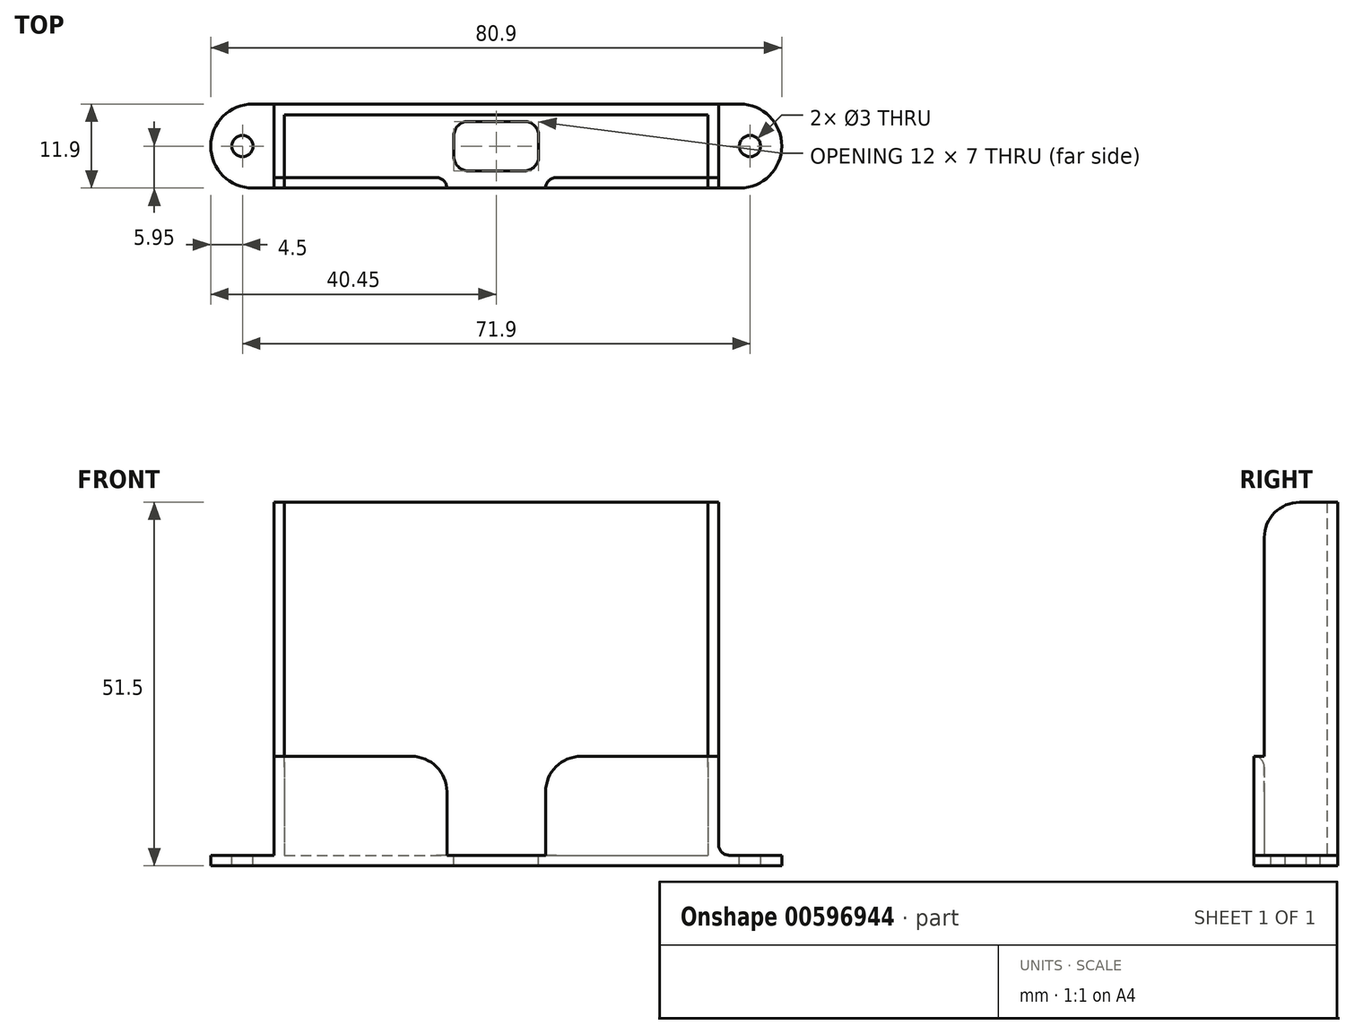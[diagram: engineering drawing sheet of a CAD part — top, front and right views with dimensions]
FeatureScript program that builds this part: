
annotation { "Feature Type Name" : "Feature", "Feature Type Description" : "" }
export const myFeature = defineFeature(function(context is Context, id is Id, definition is map)
    precondition{}
    {
        {
            assignVariable(context, id + "F0", {"name" : "THK", "anyValue" : 1.5});
        }
        {
            var Q0;
            Q0=qCreatedBy(makeId("Top.planeOp"),FACE);
            var sketch = newSketch(context, id + "F1", { "sketchPlane" : qUnion([Q0])});
            skLineSegment(sketch, "E0.bottom", {"start": v(-61.5, -1.5) * mm, "end": v(-1.5, -1.5) * mm});
            skLineSegment(sketch, "E0.top", {"start": v(-61.5, -10.4) * mm, "end": v(-1.5, -10.4) * mm});
            skLineSegment(sketch, "E0.left", {"start": v(-61.5, -1.5) * mm, "end": v(-61.5, -10.4) * mm});
            skLineSegment(sketch, "E0.right", {"start": v(-1.5, -1.5) * mm, "end": v(-1.5, -10.4) * mm});
            skLineSegment(sketch, "E1.0", {"start": v(-63, 0) * mm, "end": v(0, 0) * mm});
            skLineSegment(sketch, "E1.1", {"start": v(-63, 0) * mm, "end": v(-63, -11.9) * mm});
            skLineSegment(sketch, "E1.2", {"start": v(-63, -11.9) * mm, "end": v(0, -11.9) * mm});
            skLineSegment(sketch, "E1.3", {"start": v(0, 0) * mm, "end": v(0, -11.9) * mm});
            skLineSegment(sketch, "E2", {"start": v(-1.5, -10.4) * mm, "end": v(0, -10.4) * mm});
            skLineSegment(sketch, "E3", {"start": v(-61.5, -10.4) * mm, "end": v(-63, -10.4) * mm});
            skLineSegment(sketch, "E4", {"start": v(-31.5, -1.5) * mm, "end": v(-31.5, -10.4) * mm, "construction": true});
            skLineSegment(sketch, "E5", {"start": v(-63, 0) * mm, "end": v(-66, 0) * mm});
            skLineSegment(sketch, "E6", {"start": v(0, 0) * mm, "end": v(3, 0) * mm});
            skLineSegment(sketch, "E7", {"start": v(0, -11.9) * mm, "end": v(3, -11.9) * mm});
            skLineSegment(sketch, "E8", {"start": v(-63, -11.9) * mm, "end": v(-66, -11.9) * mm});
            skArc(sketch, "E9", {"start": v(-66, 0) * mm, "mid": v(-71.95, -5.95) * mm, "end": v(-66, -11.9) * mm});
            skArc(sketch, "E10", {"start": v(3, 0) * mm, "mid": v(8.95, -5.95) * mm, "end": v(3, -11.9) * mm});
            skLineSegment(sketch, "E11", {"start": v(-71.95, -5.95) * mm, "end": v(8.95, -5.95) * mm, "construction": true});
            skCircle(sketch, "E12", {"center": v(-67.45, -5.95) * mm, "radius": 1.5 * mm});
            skCircle(sketch, "E13.MirrorC", {"center": v(4.45, -5.95) * mm, "radius": 1.5 * mm});
            skLineSegment(sketch, "E14", {"start": v(-24.5, -10.4) * mm, "end": v(-24.5, -11.9) * mm});
            skLineSegment(sketch, "E15", {"start": v(-38.5, -10.4) * mm, "end": v(-38.5, -11.9) * mm});
            skLineSegment(sketch, "E16", {"start": v(-35.5, -2.45) * mm, "end": v(-27.5, -2.45) * mm});
            skLineSegment(sketch, "E17", {"start": v(-27.5, -9.45) * mm, "end": v(-35.5, -9.45) * mm});
            skPoint(sketch, "E18", {"position": v(-31.5, -2.45) * mm});
            skLineSegment(sketch, "E19", {"start": v(-37.5, -4.45) * mm, "end": v(-37.5, -7.45) * mm});
            skLineSegment(sketch, "E20", {"start": v(-25.5, -4.45) * mm, "end": v(-25.5, -7.45) * mm});
            skPoint(sketch, "E21.visualSharp", {"position": v(-37.5, -2.45) * mm});
            skArc(sketch, "E21.filletArc", {"start": v(-35.5, -2.45) * mm, "mid": v(-36.91, -3.04) * mm, "end": v(-37.5, -4.45) * mm});
            skPoint(sketch, "E22.visualSharp", {"position": v(-37.5, -9.45) * mm});
            skArc(sketch, "E22.filletArc", {"start": v(-37.5, -7.45) * mm, "mid": v(-36.91, -8.86) * mm, "end": v(-35.5, -9.45) * mm});
            skPoint(sketch, "E23.visualSharp", {"position": v(-25.5, -9.45) * mm});
            skArc(sketch, "E23.filletArc", {"start": v(-27.5, -9.45) * mm, "mid": v(-26.09, -8.86) * mm, "end": v(-25.5, -7.45) * mm});
            skPoint(sketch, "E24.visualSharp", {"position": v(-25.5, -2.45) * mm});
            skArc(sketch, "E24.filletArc", {"start": v(-25.5, -4.45) * mm, "mid": v(-26.09, -3.04) * mm, "end": v(-27.5, -2.45) * mm});
            skSolve(sketch);
        }
        {
            var Q0;
            Q0=makeQuery(id+"F1.imprint","IMPRINT",FACE,{"disambiguationData":[TD([[makeQuery(id+"F1.imprint","IMPRINT",EDGE,{"derivedFrom":sQuery(id+"F1.wireOp",EDGE,"E0.right")}),1.0]])]});
            var Q1;
            Q1=makeQuery(id+"F1.imprint","IMPRINT",FACE,{"disambiguationData":[TD([[makeQuery(id+"F1.imprint","IMPRINT",EDGE,{"derivedFrom":sQuery(id+"F1.wireOp",EDGE,"E0.top")}),-1.0]])]});
            var Q2;
            Q2=makeQuery(id+"F1.imprint","IMPRINT",FACE,{"disambiguationData":[TD([[makeQuery(id+"F1.imprint","IMPRINT",EDGE,{"derivedFrom":sQuery(id+"F1.wireOp",EDGE,"E0.bottom")}),1.0]])]});
            var Q3;
            Q3=makeQuery(id+"F1.imprint","IMPRINT",FACE,{"disambiguationData":[TD([[makeQuery(id+"F1.imprint","IMPRINT",EDGE,{"derivedFrom":sQuery(id+"F1.wireOp",EDGE,"E0.bottom")}),-1.0]])]});
            var Q4;
            {var subQ0=sQuery(id+"F1.wireOp",EDGE,"v1pQhFt7-J4Kf-ouM1-Mokq-JOx43GeG9Wj8");Q4=makeQuery(id+"F1.imprint","IMPRINT",FACE,{"disambiguationData":[TD([[makeQuery(id+"F1.imprint","IMPRINT",EDGE,{"derivedFrom":subQ0}),1.0]])]});}
            var Q5;
            {var subQ0=sQuery(id+"F1.wireOp",EDGE,"f7334b1f-d61c-490d-bf83-d8ae5c5b7b340.MirrorCS");Q5=makeQuery(id+"F1.imprint","IMPRINT",FACE,{"disambiguationData":[TD([[makeQuery(id+"F1.imprint","IMPRINT",EDGE,{"derivedFrom":subQ0}),-1.0]])]});}
            var Q6;
            {var subQ3=sQuery(id+"F1.wireOp",EDGE,"E5");Q6=makeQuery(id+"F1.imprint","IMPRINT",FACE,{"disambiguationData":[TD([[makeQuery(id+"F1.imprint","IMPRINT",EDGE,{"derivedFrom":subQ3}),1.0]])]});}
            var Q7;
            {var subQ0=sQuery(id+"F1.wireOp",EDGE,"E6");Q7=makeQuery(id+"F1.imprint","IMPRINT",FACE,{"disambiguationData":[TD([[makeQuery(id+"F1.imprint","IMPRINT",EDGE,{"derivedFrom":subQ0}),-1.0]])]});}
            var Q8;
            {var subQ0=sQuery(id+"F1.wireOp",EDGE,"E3");Q8=makeQuery(id+"F1.imprint","IMPRINT",FACE,{"disambiguationData":[TD([[makeQuery(id+"F1.imprint","IMPRINT",EDGE,{"derivedFrom":subQ0}),1.0]])]});}
            var Q9;
            {var subQ0=sQuery(id+"F1.wireOp",EDGE,"E2");Q9=makeQuery(id+"F1.imprint","IMPRINT",FACE,{"disambiguationData":[TD([[makeQuery(id+"F1.imprint","IMPRINT",EDGE,{"derivedFrom":subQ0}),-1.0]])]});}
            extrude(context, id + "F2", {"entities" : qUnion([Q0, Q1, Q2, Q3, Q4, Q5, Q6, Q7, Q8, Q9]), "oppositeDirection" : true, "depth" : (getVariable(context, 'THK')) * mm, "offsetDistance" : 25 * mm});
        }
        {
            var Q0;
            {var subQ0=sQuery(id+"F1.wireOp",EDGE,"E2");Q0=makeQuery(id+"F1.imprint","IMPRINT",FACE,{"disambiguationData":[TD([[makeQuery(id+"F1.imprint","IMPRINT",EDGE,{"derivedFrom":subQ0}),-1.0]])]});}
            var Q1;
            {var subQ0=sQuery(id+"F1.wireOp",EDGE,"E3");Q1=makeQuery(id+"F1.imprint","IMPRINT",FACE,{"disambiguationData":[TD([[makeQuery(id+"F1.imprint","IMPRINT",EDGE,{"derivedFrom":subQ0}),1.0]])]});}
            extrude(context, id + "F3", {"entities" : qUnion([Q0, Q1]), "operationType" : NewBodyOperationType.ADD, "depth" : 14 * mm, "offsetDistance" : 25 * mm});
        }
        {
            var Q0;
            Q0=makeQuery(id+"F1.imprint","IMPRINT",FACE,{"disambiguationData":[TD([[makeQuery(id+"F1.imprint","IMPRINT",EDGE,{"derivedFrom":sQuery(id+"F1.wireOp",EDGE,"E0.right")}),1.0]])]});
            extrude(context, id + "F4", {"entities" : qUnion([Q0]), "operationType" : NewBodyOperationType.ADD, "depth" : 50 * mm, "offsetDistance" : 25 * mm});
        }
        {
            var Q0;
            Q0=makeQuery(id+"F4.opExtrude","CAP_EDGE",EDGE,{"disambiguationData":[OSD([sQuery(id+"F1.wireOp",EDGE,"E3")])],"isStart":false});
            var Q1;
            Q1=makeQuery(id+"F4.opExtrude","CAP_EDGE",EDGE,{"disambiguationData":[OSD([sQuery(id+"F1.wireOp",EDGE,"E2")])],"isStart":false});
            var Q2;
            Q2=makeQuery(id+"F3.opExtrude","CAP_EDGE",EDGE,{"disambiguationData":[OSD([sQuery(id+"F1.wireOp",EDGE,"E14")])],"isStart":false});
            var Q3;
            Q3=makeQuery(id+"F3.opExtrude","CAP_EDGE",EDGE,{"disambiguationData":[OSD([sQuery(id+"F1.wireOp",EDGE,"E15")])],"isStart":false});
            fillet(context, id + "F5", {"entities" : qUnion([Q0, Q1, Q2, Q3]), "radius" : 5 * mm, "tangentPropagation" : true, "allowEdgeOverflow" : false});
        }
        {
            var Q0;
            {var subQ0=sQuery(id+"F1.wireOp",EDGE,"E3");var subQ1=sQuery(id+"F1.wireOp",EDGE,"E0.top");Q0=makeQuery(id+"F4.boolean.opBoolean","SPLIT",EDGE,{"disambiguationData":[topologyDisambiguationEdgeConnected([makeQuery(id+"F4.opExtrude","SWEPT_FACE",FACE,{"disambiguationData":[OSD([subQ0])]})])],"derivedFrom":makeQuery(id+"F3.opExtrude","CAP_EDGE",EDGE,{"disambiguationData":[OSD([subQ1,subQ0])],"isStart":false})});}
            var Q1;
            {var subQ0=sQuery(id+"F1.wireOp",EDGE,"E1.1");Q1=makeQuery(id+"F4.boolean.opBoolean","MERGE",EDGE,{"derivedFrom":[makeQuery(id+"F3.opExtrude","CAP_EDGE",EDGE,{"disambiguationData":[OSD([subQ0])],"isStart":true}),makeQuery(id+"F4.opExtrude","CAP_EDGE",EDGE,{"disambiguationData":[OSD([subQ0])],"isStart":true})]});}
            var Q2;
            {var subQ0=sQuery(id+"F1.wireOp",EDGE,"E2");var subQ1=sQuery(id+"F1.wireOp",EDGE,"E0.top");Q2=makeQuery(id+"F4.boolean.opBoolean","SPLIT",EDGE,{"disambiguationData":[topologyDisambiguationEdgeConnected([makeQuery(id+"F4.opExtrude","SWEPT_FACE",FACE,{"disambiguationData":[OSD([subQ0])]})])],"derivedFrom":makeQuery(id+"F3.opExtrude","CAP_EDGE",EDGE,{"disambiguationData":[OSD([subQ1,subQ0])],"isStart":false})});}
            var Q3;
            {var subQ0=sQuery(id+"F1.wireOp",EDGE,"E1.3");Q3=makeQuery(id+"F4.boolean.opBoolean","MERGE",EDGE,{"derivedFrom":[makeQuery(id+"F3.opExtrude","CAP_EDGE",EDGE,{"disambiguationData":[OSD([subQ0])],"isStart":true}),makeQuery(id+"F4.opExtrude","CAP_EDGE",EDGE,{"disambiguationData":[OSD([subQ0])],"isStart":true})]});}
            fillet(context, id + "F6", {"entities" : qUnion([Q0, Q1, Q2, Q3]), "radius" : (getVariable(context, 'THK')) * mm, "tangentPropagation" : true, "allowEdgeOverflow" : false});
        }
    });
